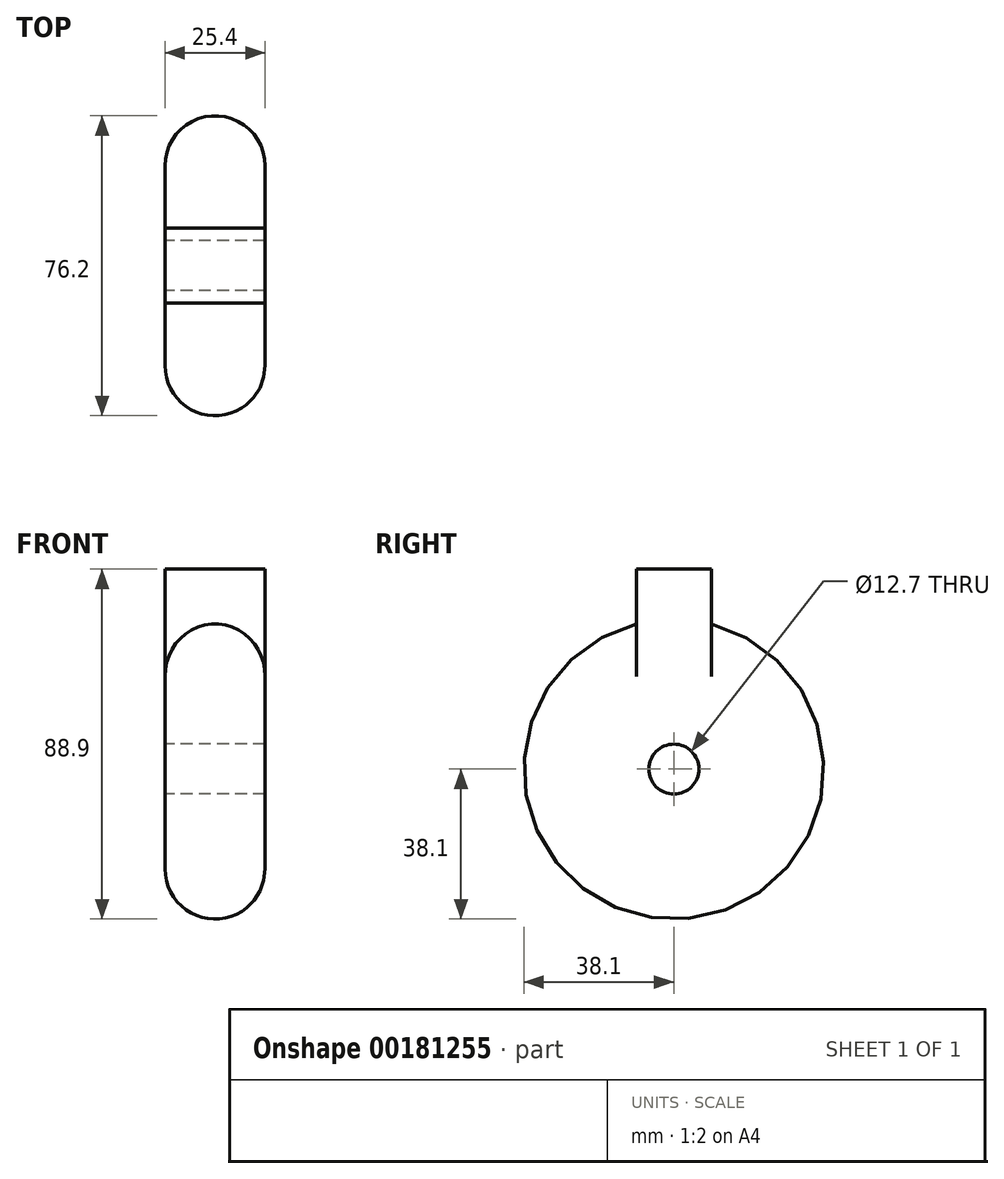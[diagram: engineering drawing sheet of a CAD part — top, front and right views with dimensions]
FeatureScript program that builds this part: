
annotation { "Feature Type Name" : "Feature", "Feature Type Description" : "" }
export const myFeature = defineFeature(function(context is Context, id is Id, definition is map)
    precondition{}
    {
        {
            var Q0;
            Q0=qCreatedBy(makeId("Right.planeOp"),FACE);
            var sketch = newSketch(context, id + "F0", { "sketchPlane" : qUnion([Q0])});
            skCircle(sketch, "E0", {"center": v(0, 0) * mm, "radius": 38.1 * mm});
            skCircle(sketch, "E1", {"center": v(0, 0) * mm, "radius": 6.35 * mm});
            skSolve(sketch);
        }
        {
            var Q0;
            Q0 = qSketchRegion(id + "F0", true);
            extrude(context, id + "F1", {"entities" : qUnion([Q0]), "depth" : 25.4 * mm});
        }
        {
            var Q0;
            Q0=makeQuery(id+"F1.opExtrude","CAP_EDGE",EDGE,{"disambiguationData":[OSD([sQuery(id+"F0.wireOp",EDGE,"E0")])],"isStart":true});
            var Q1;
            Q1=makeQuery(id+"F1.opExtrude","CAP_EDGE",EDGE,{"disambiguationData":[OSD([sQuery(id+"F0.wireOp",EDGE,"E0")])],"isStart":false});
            fillet(context, id + "F2", {"entities" : qUnion([Q0, Q1]), "radius" : 12.7 * mm, "tangentPropagation" : true, "allowEdgeOverflow" : false});
        }
        {
            var Q0;
            Q0=makeQuery(id+"F1.opExtrude","CAP_FACE",FACE,{"disambiguationData":[OSD([sQuery(id+"F0.wireOp",EDGE,"E0"),sQuery(id+"F0.wireOp",EDGE,"E1")])],"isStart":false});
            var sketch = newSketch(context, id + "F3", { "sketchPlane" : qUnion([Q0])});
            skLineSegment(sketch, "E2", {"start": v(0, 0) * mm, "end": v(0, -12.7) * mm});
            skLineSegment(sketch, "E3", {"start": v(0, -12.7) * mm, "end": v(-9.53, -12.7) * mm});
            skLineSegment(sketch, "E4.bottom", {"start": v(-9.52, -12.7) * mm, "end": v(9.52, -12.7) * mm});
            skLineSegment(sketch, "E4.top", {"start": v(-9.53, 50.8) * mm, "end": v(9.52, 50.8) * mm});
            skLineSegment(sketch, "E4.left", {"start": v(-9.53, -12.7) * mm, "end": v(-9.53, 50.8) * mm});
            skLineSegment(sketch, "E4.right", {"start": v(9.52, -12.7) * mm, "end": v(9.52, 50.8) * mm});
            skSolve(sketch);
        }
        {
            var Q0;
            {var subQ0=sQuery(id+"F3.wireOp",EDGE,"E4.top");Q0=makeQuery(id+"F3.imprint","IMPRINT",FACE,{"disambiguationData":[TD([[makeQuery(id+"F3.imprint","IMPRINT",EDGE,{"derivedFrom":subQ0}),-1.0]])]});}
            var Q1;
            {var subQ3=sQuery(id+"F0.wireOp",EDGE,"E1");Q1=makeQuery(id+"F3.imprint","IMPRINT",FACE,{"disambiguationData":[TD([[makeQuery(id+"F3.imprint","IMPRINT",EDGE,{"derivedFrom":makeQuery(id+"F1.opExtrude","CAP_EDGE",EDGE,{"disambiguationData":[OSD([subQ3])],"isStart":false})}),-1.0]])]});}
            extrude(context, id + "F4", {"entities" : qUnion([Q0, Q1]), "operationType" : NewBodyOperationType.ADD, "oppositeDirection" : true, "depth" : 25.4 * mm});
        }
    });
